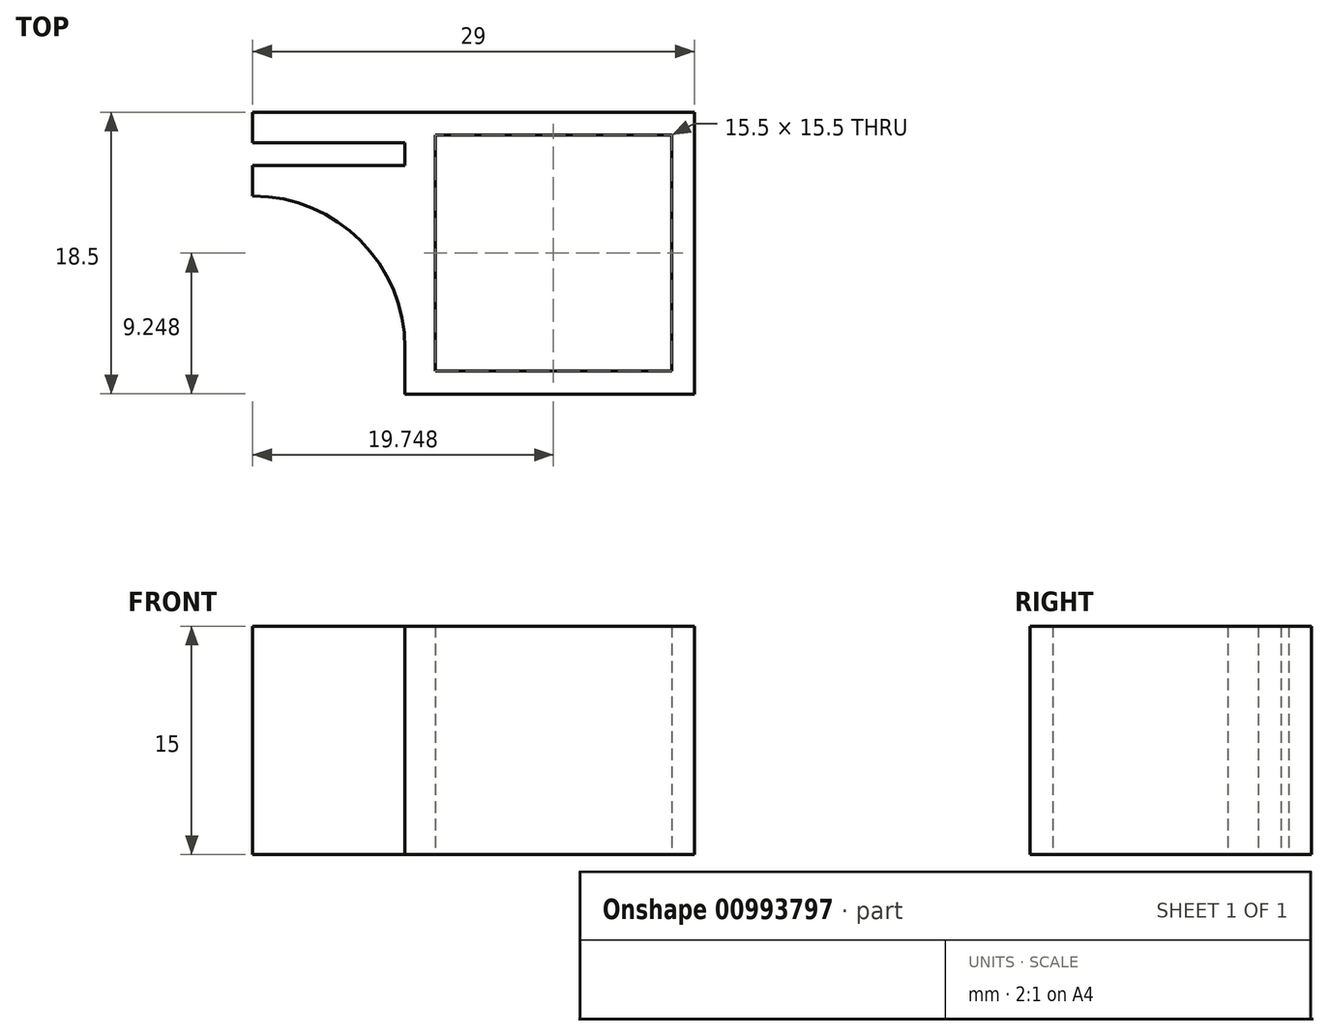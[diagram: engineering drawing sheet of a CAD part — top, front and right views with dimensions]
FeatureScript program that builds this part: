
annotation { "Feature Type Name" : "Feature", "Feature Type Description" : "" }
export const myFeature = defineFeature(function(context is Context, id is Id, definition is map)
    precondition{}
    {
        {
            var Q0;
            Q0=qCreatedBy(makeId("Top.planeOp"),FACE);
            var sketch = newSketch(context, id + "F0", { "sketchPlane" : qUnion([Q0])});
            skLineSegment(sketch, "E0", {"start": v(-8.12, 3.48) * mm, "end": v(-23.62, 3.48) * mm});
            skLineSegment(sketch, "E1", {"start": v(-25.62, -7.02) * mm, "end": v(-25.62, -0.52) * mm});
            skLineSegment(sketch, "E2", {"start": v(-25.62, -0.52) * mm, "end": v(-35.62, -0.52) * mm});
            skLineSegment(sketch, "E3", {"start": v(-35.62, -0.52) * mm, "end": v(-35.62, 1.48) * mm});
            skLineSegment(sketch, "E4", {"start": v(-35.62, 1.48) * mm, "end": v(-25.62, 1.48) * mm});
            skLineSegment(sketch, "E5", {"start": v(-25.62, 1.48) * mm, "end": v(-25.62, 2.98) * mm});
            skLineSegment(sketch, "E6", {"start": v(-25.62, 2.98) * mm, "end": v(-35.62, 2.98) * mm});
            skLineSegment(sketch, "E7", {"start": v(-35.62, 2.98) * mm, "end": v(-35.62, 4.98) * mm});
            skLineSegment(sketch, "E8", {"start": v(-35.62, 4.98) * mm, "end": v(-6.62, 4.98) * mm});
            skLineSegment(sketch, "E9", {"start": v(-6.62, 4.98) * mm, "end": v(-6.62, -8.3) * mm});
            skLineSegment(sketch, "E10", {"start": v(-8.12, -12.02) * mm, "end": v(-23.62, -12.02) * mm});
            skLineSegment(sketch, "E11", {"start": v(-25.62, -7.02) * mm, "end": v(-25.62, -13.52) * mm});
            skLineSegment(sketch, "E12", {"start": v(-25.62, -13.52) * mm, "end": v(-6.62, -13.52) * mm});
            skLineSegment(sketch, "E13", {"start": v(-6.62, -13.52) * mm, "end": v(-6.62, -8.3) * mm});
            skLineSegment(sketch, "E14", {"start": v(-8.12, -12.02) * mm, "end": v(-8.12, 3.48) * mm});
            skLineSegment(sketch, "E15", {"start": v(-23.62, -12.02) * mm, "end": v(-23.62, 3.48) * mm});
            skSolve(sketch);
        }
        {
            var Q0;
            Q0=makeQuery(id+"F0.imprint","IMPRINT",FACE,{"disambiguationData":[TD([[makeQuery(id+"F0.imprint","IMPRINT",EDGE,{"derivedFrom":sQuery(id+"F0.wireOp",EDGE,"dk07c19K-g7GK-wDqm-Y6yp-qfXFjsn0dxpM")}),-1.0]])]});
            var Q1;
            Q1=makeQuery(id+"F0.imprint","IMPRINT",FACE,{"disambiguationData":[TD([[makeQuery(id+"F0.imprint","IMPRINT",EDGE,{"derivedFrom":sQuery(id+"F0.wireOp",EDGE,"E0")}),-1.0]])]});
            extrude(context, id + "F1", {"entities" : qUnion([Q0, Q1]), "depth" : 15 * mm, "offsetDistance" : 25 * mm, "symmetric" : true});
        }
        {
            var Q0;
            Q0=makeQuery(id+"F1.opExtrude","SWEPT_EDGE",EDGE,{"disambiguationData":[OSD([sQuery(id+"F0.wireOp",EDGE,"E1"),sQuery(id+"F0.wireOp",EDGE,"E2")])]});
            fillet(context, id + "F2", {"entities" : qUnion([Q0]), "tangentPropagation" : true, "radius" : 10 * mm, "defaultsChanged" : true, "vertexSettings" : [], "allowEdgeOverflow" : false});
        }
    });
